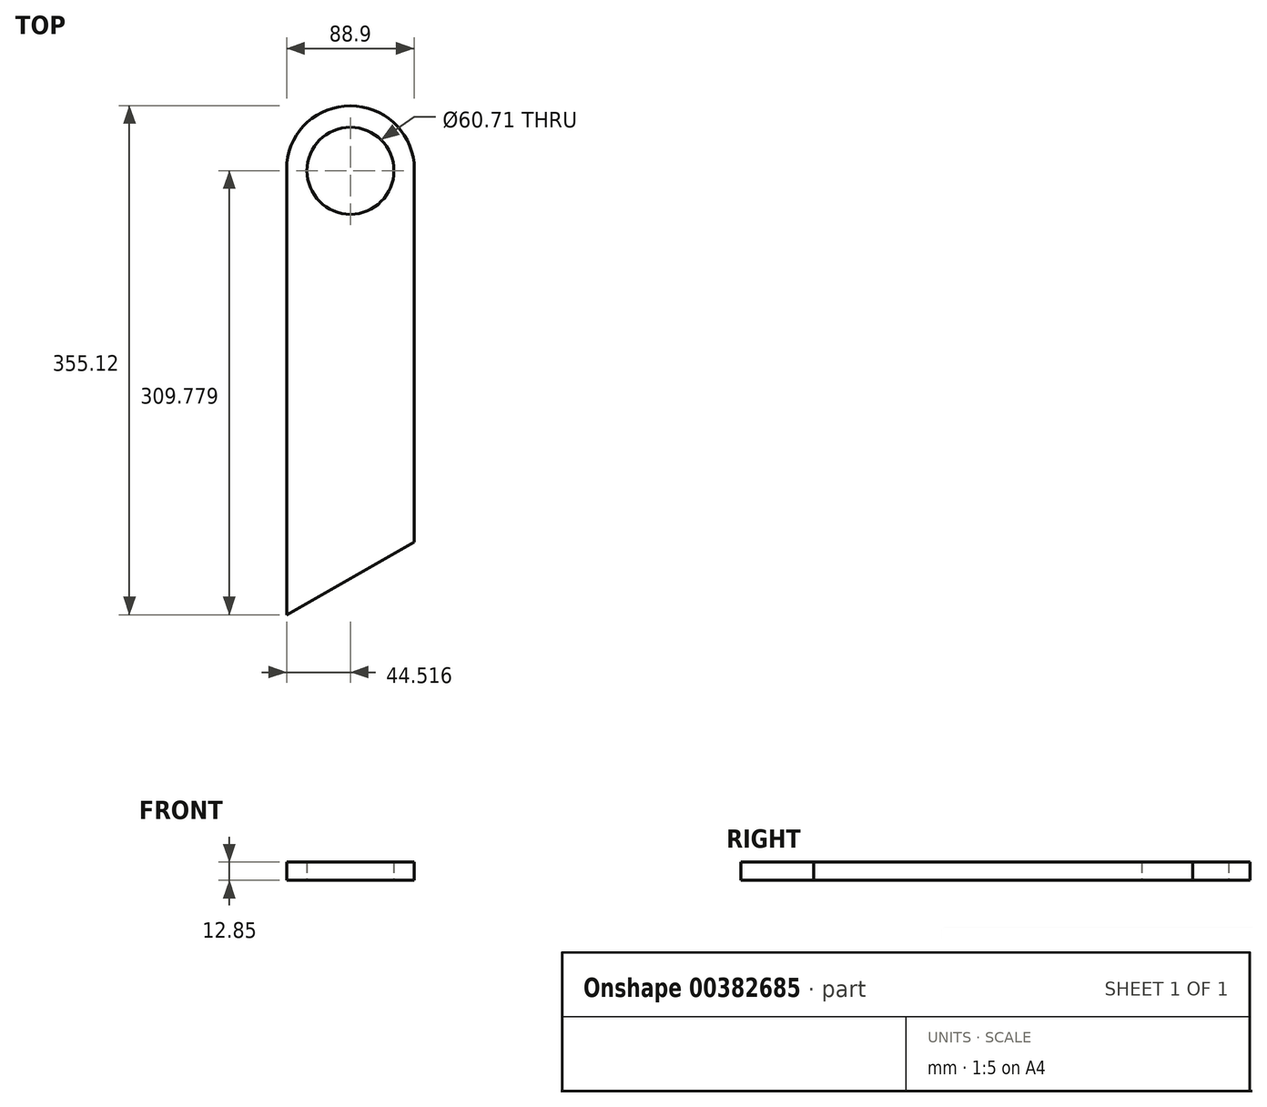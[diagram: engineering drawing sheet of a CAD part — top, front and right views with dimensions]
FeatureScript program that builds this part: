
annotation { "Feature Type Name" : "Feature", "Feature Type Description" : "" }
export const myFeature = defineFeature(function(context is Context, id is Id, definition is map)
    precondition{}
    {
        {
            var Q0;
            Q0=qCreatedBy(makeId("Top.planeOp"),FACE);
            var sketch = newSketch(context, id + "F0", { "sketchPlane" : qUnion([Q0])});
            skLineSegment(sketch, "E0.bottom", {"start": v(-21.34, -167.78) * mm, "end": v(-110.24, -167.78) * mm});
            skLineSegment(sketch, "E0.top", {"start": v(-21.34, 187.82) * mm, "end": v(-110.24, 187.82) * mm});
            skLineSegment(sketch, "E0.left", {"start": v(-21.34, -167.78) * mm, "end": v(-21.34, 187.82) * mm});
            skLineSegment(sketch, "E0.right", {"start": v(-110.24, -167.78) * mm, "end": v(-110.24, 187.82) * mm});
            skSolve(sketch);
        }
        {
            var Q0;
            Q0=makeQuery(id+"F0.imprint","IMPRINT",FACE,{"disambiguationData":[TD([[makeQuery(id+"F0.imprint","IMPRINT",EDGE,{"derivedFrom":sQuery(id+"F0.wireOp",EDGE,"E0.bottom")}),-1.0]])]});
            var sketch = newSketch(context, id + "F1", { "sketchPlane" : qUnion([Q0])});
            skCircle(sketch, "E1", {"center": v(-65.72, 142) * mm, "radius": 30.35 * mm});
            skSolve(sketch);
        }
        {
            var Q0;
            Q0=makeQuery(id+"F0.imprint","IMPRINT",FACE,{"disambiguationData":[TD([[makeQuery(id+"F0.imprint","IMPRINT",EDGE,{"derivedFrom":sQuery(id+"F0.wireOp",EDGE,"E0.bottom")}),-1.0]])]});
            var sketch = newSketch(context, id + "F2", { "sketchPlane" : qUnion([Q0])});
            skLineSegment(sketch, "E2.0.0", {"start": v(-21.34, -167.78) * mm, "end": v(-21.34, 187.82) * mm});
            skLineSegment(sketch, "E2.0.2", {"start": v(-110.24, 187.82) * mm, "end": v(-110.24, -167.78) * mm});
            skLineSegment(sketch, "E2.0.3", {"start": v(-110.24, -167.78) * mm, "end": v(-21.34, -167.78) * mm});
            skArc(sketch, "E3", {"start": v(-21.34, 147.3) * mm, "mid": v(-65.79, 187.34) * mm, "end": v(-110.24, 147.3) * mm});
            skSolve(sketch);
        }
        {
            var Q0;
            Q0=makeQuery(id+"F1.imprint","IMPRINT",FACE,{"disambiguationData":[TD([[makeQuery(id+"F1.imprint","IMPRINT",EDGE,{"derivedFrom":sQuery(id+"F1.wireOp",EDGE,"E1")}),-1.0]])]});
            var sketch = newSketch(context, id + "F3", { "sketchPlane" : qUnion([Q0])});
            skArc(sketch, "E4.0", {"start": v(-21.34, 147.3) * mm, "mid": v(-65.79, 187.34) * mm, "end": v(-110.24, 147.3) * mm});
            skCircle(sketch, "E5.0", {"center": v(-65.72, 142) * mm, "radius": 30.35 * mm});
            skLineSegment(sketch, "E6.0", {"start": v(-110.24, -167.78) * mm, "end": v(-110.24, 187.82) * mm});
            skLineSegment(sketch, "E7.0", {"start": v(-21.34, -167.78) * mm, "end": v(-21.34, 187.82) * mm});
            skLineSegment(sketch, "E8.0", {"start": v(-21.34, -167.78) * mm, "end": v(-110.24, -167.78) * mm});
            skSolve(sketch);
        }
        {
            var Q0;
            {var subQ2=sQuery(id+"F3.wireOp",EDGE,"E4.0");Q0=makeQuery(id+"F3.imprint","IMPRINT",FACE,{"disambiguationData":[TD([[makeQuery(id+"F3.imprint","IMPRINT",EDGE,{"derivedFrom":subQ2}),1.0]])]});}
            var sketch = newSketch(context, id + "F4", { "sketchPlane" : qUnion([Q0])});
            skArc(sketch, "E9.0.1", {"start": v(-21.34, 147.3) * mm, "mid": v(-65.79, 187.34) * mm, "end": v(-110.24, 147.3) * mm});
            skLineSegment(sketch, "E10", {"start": v(-110.24, -167.78) * mm, "end": v(-21.34, -116.98) * mm});
            skSolve(sketch);
        }
        {
            var Q0;
            {var subQ4=sQuery(id+"F4.wireOp",EDGE,"E9.0.1");Q0=makeQuery(id+"F4.imprint","IMPRINT",FACE,{"disambiguationData":[TD([[makeQuery(id+"F4.imprint","IMPRINT",EDGE,{"derivedFrom":subQ4}),1.0]])]});}
            extrude(context, id + "F5", {"entities" : qUnion([Q0]), "depth" : 12.85 * mm});
        }
    });
